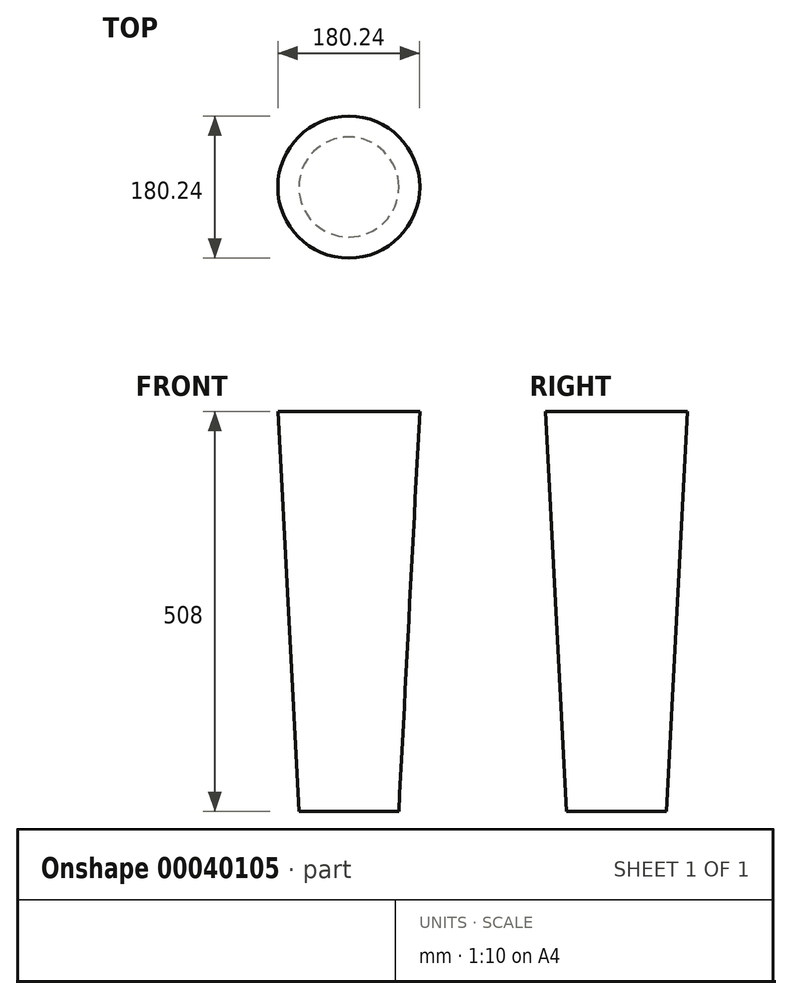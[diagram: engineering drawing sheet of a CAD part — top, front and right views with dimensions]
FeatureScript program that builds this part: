
annotation { "Feature Type Name" : "Feature", "Feature Type Description" : "" }
export const myFeature = defineFeature(function(context is Context, id is Id, definition is map)
    precondition{}
    {
        {
            var Q0;
            Q0=qCreatedBy(makeId("Top.planeOp"),FACE);
            var sketch = newSketch(context, id + "F0", { "sketchPlane" : qUnion([Q0])});
            skCircle(sketch, "E0", {"center": v(0, 0) * mm, "radius": 63.5 * mm});
            skSolve(sketch);
        }
        {
            var Q0;
            Q0=makeQuery(id+"F0.imprint","IMPRINT",FACE,{"disambiguationData":[TD([[makeQuery(id+"F0.imprint","IMPRINT",EDGE,{"derivedFrom":sQuery(id+"F0.wireOp",EDGE,"E0")}),1.0]])]});
            extrude(context, id + "F1", {"entities" : qUnion([Q0]), "depth" : 508 * mm, "hasDraft" : true, "draftAngle" : 3 * degree});
        }
    });
